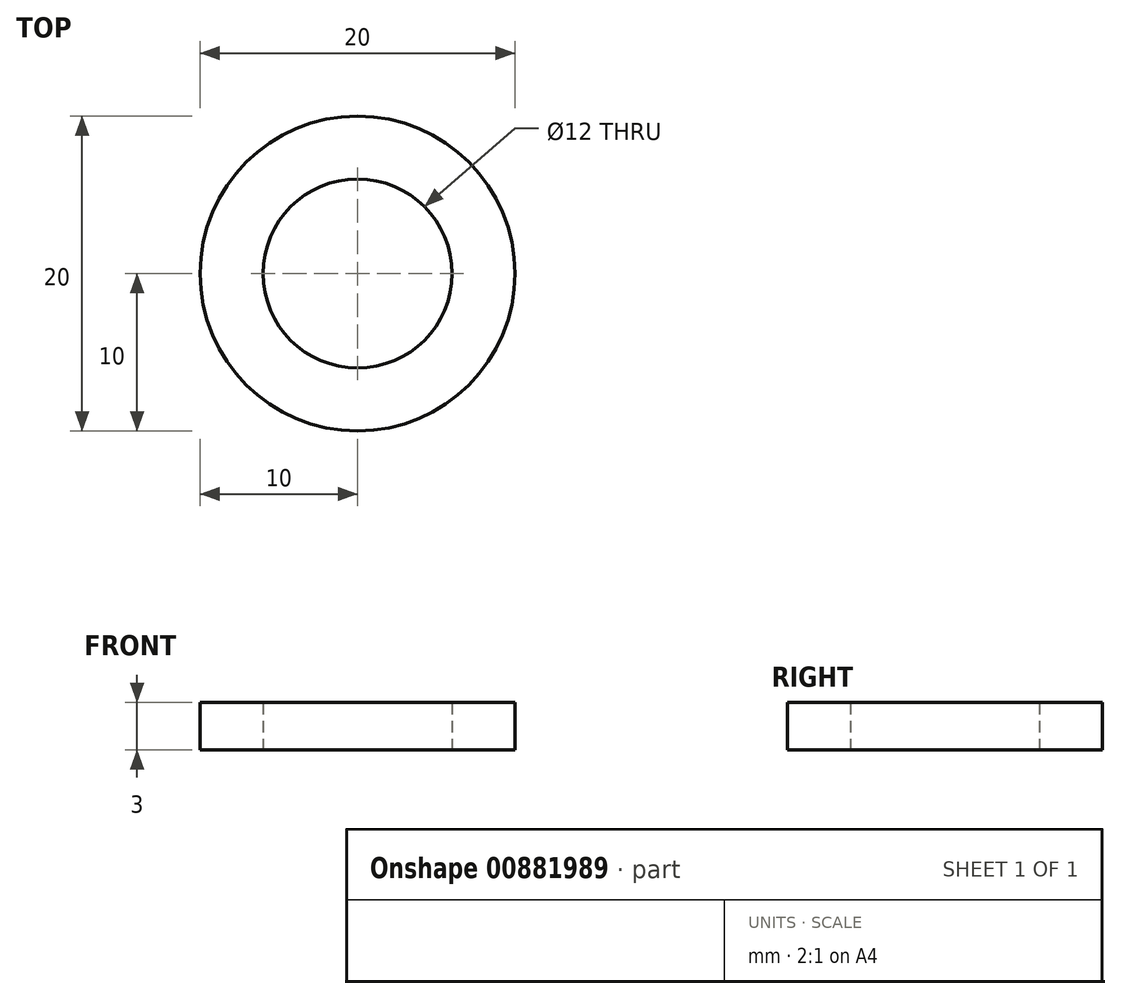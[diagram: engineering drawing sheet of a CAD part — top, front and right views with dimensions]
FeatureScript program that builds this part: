
annotation { "Feature Type Name" : "Feature", "Feature Type Description" : "" }
export const myFeature = defineFeature(function(context is Context, id is Id, definition is map)
    precondition{}
    {
        {
            var Q0;
            Q0=qCreatedBy(makeId("Top.planeOp"),FACE);
            var sketch = newSketch(context, id + "F0", { "sketchPlane" : qUnion([Q0])});
            skCircle(sketch, "E0", {"center": v(0, 0) * mm, "radius": 6 * mm});
            skCircle(sketch, "E1", {"center": v(0, 0) * mm, "radius": 10 * mm});
            skSolve(sketch);
        }
        {
            var Q0;
            Q0 = qSketchRegion(id + "F0", true);
            extrude(context, id + "F1", {"entities" : qUnion([Q0]), "depth" : 3 * mm, "offsetDistance" : 25 * mm});
        }
    });
